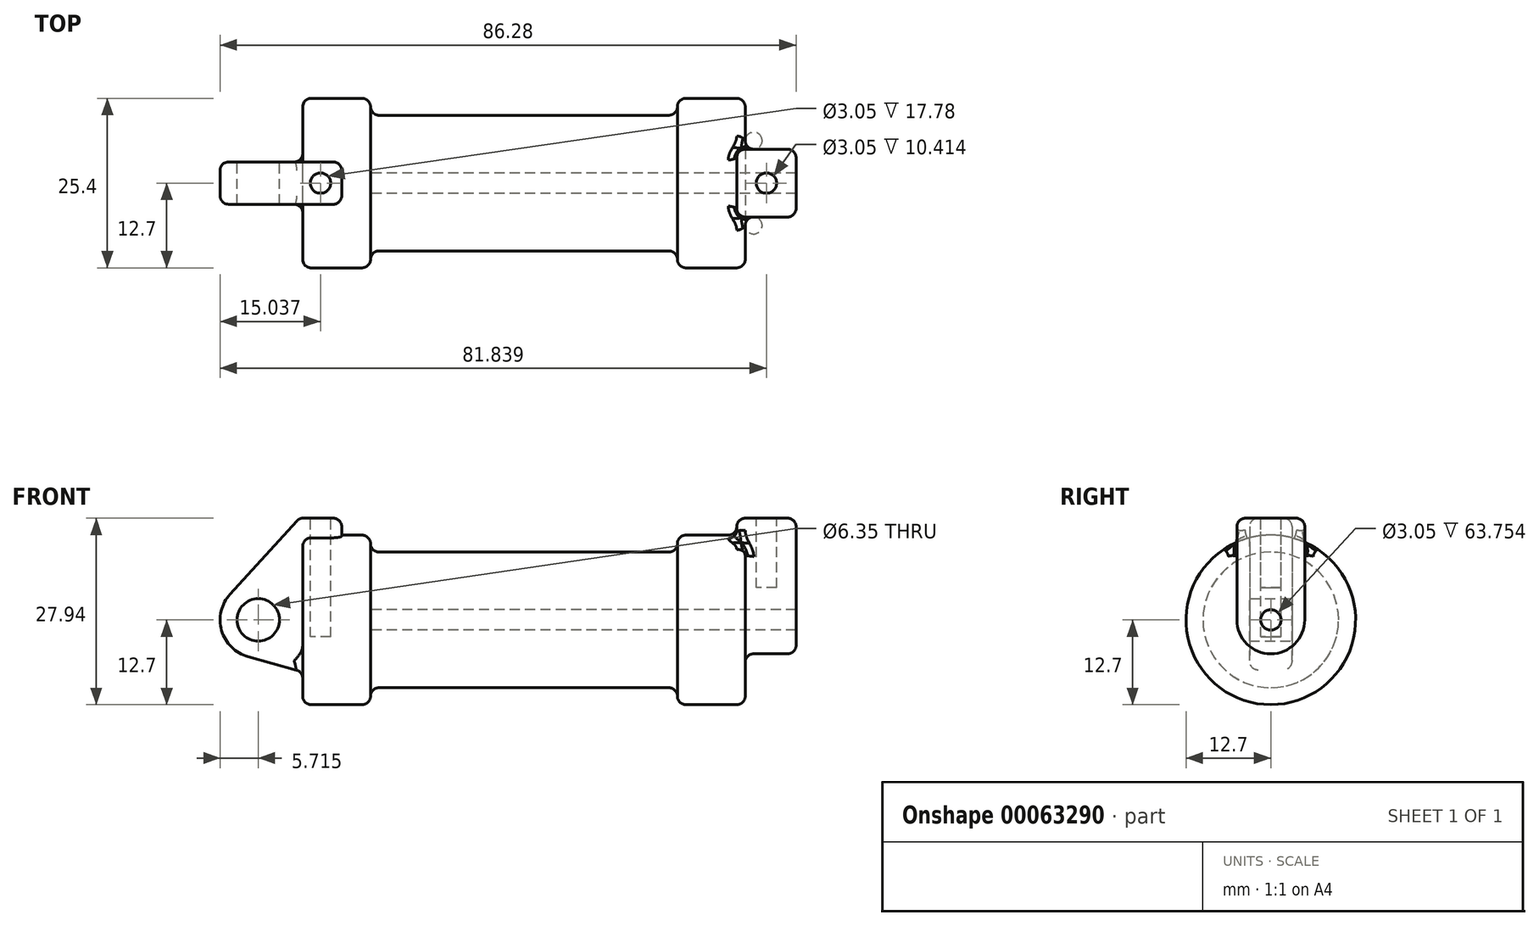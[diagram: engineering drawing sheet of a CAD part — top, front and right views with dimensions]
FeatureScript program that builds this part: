
annotation { "Feature Type Name" : "Feature", "Feature Type Description" : "" }
export const myFeature = defineFeature(function(context is Context, id is Id, definition is map)
    precondition{}
    {
        {
            var Q0;
            Q0=qCreatedBy(makeId("Front.planeOp"),FACE);
            var sketch = newSketch(context, id + "F0", { "sketchPlane" : qUnion([Q0])});
            skLineSegment(sketch, "E0", {"start": v(0, 0) * mm, "end": v(0, 12.7) * mm});
            skLineSegment(sketch, "E1", {"start": v(0, 12.7) * mm, "end": v(10.16, 12.7) * mm});
            skLineSegment(sketch, "E2", {"start": v(10.16, 12.7) * mm, "end": v(10.16, 10.16) * mm});
            skLineSegment(sketch, "E3", {"start": v(10.16, 10.16) * mm, "end": v(56.13, 10.16) * mm});
            skLineSegment(sketch, "E4", {"start": v(56.13, 10.16) * mm, "end": v(56.13, 12.7) * mm});
            skLineSegment(sketch, "E5", {"start": v(56.13, 12.7) * mm, "end": v(66.3, 12.7) * mm});
            skLineSegment(sketch, "E6", {"start": v(66.3, 12.7) * mm, "end": v(66.3, 0) * mm});
            skLineSegment(sketch, "E7", {"start": v(66.3, 0) * mm, "end": v(0, 0) * mm});
            skLineSegment(sketch, "E8", {"start": v(5.84, 15.24) * mm, "end": v(-0.5, 15.24) * mm});
            skLineSegment(sketch, "E9", {"start": v(-0.5, 15.24) * mm, "end": v(-10.88, 3.85) * mm});
            skLineSegment(sketch, "E10", {"start": v(0, 0) * mm, "end": v(-6.65, 0) * mm});
            skCircle(sketch, "E11", {"center": v(-6.65, 0) * mm, "radius": 5.72 * mm});
            skCircle(sketch, "E12", {"center": v(-6.65, 0) * mm, "radius": 3.18 * mm});
            skLineSegment(sketch, "E13", {"start": v(5.84, 15.24) * mm, "end": v(5.84, -9.4) * mm});
            skLineSegment(sketch, "E14", {"start": v(5.84, -9.4) * mm, "end": v(-8.18, -5.5) * mm});
            skSolve(sketch);
        }
        {
            var Q0;
            {var subQ0=sQuery(id+"F0.wireOp",EDGE,"E2");Q0=makeQuery(id+"F0.imprint","IMPRINT",FACE,{"disambiguationData":[TD([[makeQuery(id+"F0.imprint","IMPRINT",EDGE,{"derivedFrom":subQ0}),-1.0]])]});}
            var Q1;
            {var subQ0=sQuery(id+"F0.wireOp",EDGE,"E0");Q1=makeQuery(id+"F0.imprint","IMPRINT",FACE,{"disambiguationData":[TD([[makeQuery(id+"F0.imprint","IMPRINT",EDGE,{"derivedFrom":subQ0}),-1.0]])]});}
            var Q2;
            Q2=sQuery(id+"F0.wireOp",EDGE,"E0");
            var Q3;
            Q3=sQuery(id+"F0.wireOp",EDGE,"E1");
            var Q4;
            Q4=sQuery(id+"F0.wireOp",EDGE,"E4");
            var Q5;
            Q5=sQuery(id+"F0.wireOp",EDGE,"E5");
            var Q6;
            Q6=sQuery(id+"F0.wireOp",EDGE,"E6");
            var Q7;
            Q7=sQuery(id+"F0.wireOp",EDGE,"E2");
            var Q8;
            Q8=sQuery(id+"F0.wireOp",EDGE,"E3");
            var Q9;
            Q9=sQuery(id+"F0.wireOp",EDGE,"E7");
            var Q10;
            Q10=sQuery(id+"F0.wireOp",EDGE,"E7");
            revolve(context, id + "F1", {"entities" : qUnion([Q0, Q1]), "surfaceEntities" : qUnion([Q2, Q3, Q4, Q5, Q6, Q7, Q8, Q9]), "axis" : qUnion([Q10]), "revolveType" : RevolveType.FULL});
        }
        {
            var Q0;
            {var subQ3=sQuery(id+"F0.wireOp",EDGE,"E0");Q0=makeQuery(id+"F0.imprint","IMPRINT",FACE,{"disambiguationData":[TD([[makeQuery(id+"F0.imprint","IMPRINT",EDGE,{"derivedFrom":subQ3}),1.0]])]});}
            var Q1;
            {var subQ0=sQuery(id+"F0.wireOp",EDGE,"E14");Q1=makeQuery(id+"F0.imprint","IMPRINT",FACE,{"disambiguationData":[TD([[makeQuery(id+"F0.imprint","IMPRINT",EDGE,{"derivedFrom":subQ0}),-1.0]])]});}
            var Q2;
            {var subQ4=sQuery(id+"F0.wireOp",EDGE,"E12");Q2=makeQuery(id+"F0.imprint","IMPRINT",FACE,{"disambiguationData":[TD([[makeQuery(id+"F0.imprint","IMPRINT",EDGE,{"derivedFrom":subQ4}),-1.0]])]});}
            var Q3;
            {var subQ0=sQuery(id+"F0.wireOp",EDGE,"E0");Q3=makeQuery(id+"F0.imprint","IMPRINT",FACE,{"disambiguationData":[TD([[makeQuery(id+"F0.imprint","IMPRINT",EDGE,{"derivedFrom":subQ0}),-1.0]])]});}
            extrude(context, id + "F2", {"entities" : qUnion([Q0, Q1, Q2, Q3]), "operationType" : NewBodyOperationType.ADD, "endBound" : BoundingType.SYMMETRIC, "depth" : 6.35 * mm});
        }
        {
            var Q0;
            Q0=makeQuery(id+"F1.opRevolve","SWEPT_FACE",FACE,{"disambiguationData":[OSD([sQuery(id+"F0.wireOp",EDGE,"E6")])]});
            var sketch = newSketch(context, id + "F3", { "sketchPlane" : qUnion([Q0])});
            skCircle(sketch, "E15", {"center": v(0, 0) * mm, "radius": 1.52 * mm});
            skCircle(sketch, "E16", {"center": v(0, 0) * mm, "radius": 5.08 * mm});
            skLineSegment(sketch, "E17", {"start": v(-5.08, 0) * mm, "end": v(-5.08, 15.24) * mm});
            skLineSegment(sketch, "E18", {"start": v(5.08, 0) * mm, "end": v(5.08, 15.24) * mm});
            skLineSegment(sketch, "E19", {"start": v(-5.08, 15.24) * mm, "end": v(5.08, 15.24) * mm});
            skSolve(sketch);
        }
        {
            var Q0;
            Q0 = qSketchRegion(id + "F3", true);
            extrude(context, id + "F4", {"entities" : qUnion([Q0]), "operationType" : NewBodyOperationType.ADD, "depth" : 7.62 * mm});
        }
        {
            var Q0;
            Q0 = qSketchRegion(id + "F3", true);
            extrude(context, id + "F5", {"entities" : qUnion([Q0]), "operationType" : NewBodyOperationType.ADD, "oppositeDirection" : true, "depth" : 1.27 * mm});
        }
        {
            var Q0;
            Q0=makeQuery(id+"F3.imprint","IMPRINT",FACE,{"disambiguationData":[TD([[makeQuery(id+"F3.imprint","IMPRINT",EDGE,{"derivedFrom":sQuery(id+"F3.wireOp",EDGE,"E15")}),1.0]])]});
            var Q1;
            Q1=makeQuery(id+"F1.opRevolve","SWEPT_FACE",FACE,{"disambiguationData":[OSD([sQuery(id+"F0.wireOp",EDGE,"E2")])]});
            extrude(context, id + "F6", {"entities" : qUnion([Q0]), "operationType" : NewBodyOperationType.REMOVE, "endBound" : BoundingType.UP_TO_SURFACE, "oppositeDirection" : true, "endBoundEntityFace" : qUnion([Q1]), "depth" : 25.4 * mm});
        }
        {
            var Q0;
            Q0=makeQuery(id+"F2.opExtrude","SWEPT_FACE",FACE,{"disambiguationData":[OSD([sQuery(id+"F0.wireOp",EDGE,"E8")])]});
            var sketch = newSketch(context, id + "F7", { "sketchPlane" : qUnion([Q0])});
            skLineSegment(sketch, "E20", {"start": v(-0.5, 0) * mm, "end": v(5.84, 0) * mm, "construction": true});
            skLineSegment(sketch, "E21", {"start": v(2.67, -3.18) * mm, "end": v(2.67, 3.18) * mm, "construction": true});
            skCircle(sketch, "E22", {"center": v(2.67, 0) * mm, "radius": 1.52 * mm});
            skSolve(sketch);
        }
        {
            var Q0;
            Q0 = qSketchRegion(id + "F7", true);
            extrude(context, id + "F8", {"entities" : qUnion([Q0]), "operationType" : NewBodyOperationType.REMOVE, "oppositeDirection" : true, "depth" : 17.78 * mm});
        }
        {
            var Q0;
            {var subQ0=sQuery(id+"F3.wireOp",EDGE,"E19");Q0=makeQuery(id+"F5.boolean.opBoolean","MERGE",FACE,{"derivedFrom":[makeQuery(id+"F4.opExtrude","SWEPT_FACE",FACE,{"disambiguationData":[OSD([subQ0])]}),makeQuery(id+"F5.opExtrude","SWEPT_FACE",FACE,{"disambiguationData":[OSD([subQ0])]})]});}
            var sketch = newSketch(context, id + "F9", { "sketchPlane" : qUnion([Q0])});
            skLineSegment(sketch, "E23", {"start": v(65.02, 0) * mm, "end": v(73.91, 0) * mm, "construction": true});
            skCircle(sketch, "E24", {"center": v(69.47, 0) * mm, "radius": 1.52 * mm});
            skSolve(sketch);
        }
        {
            var Q0;
            Q0 = qSketchRegion(id + "F9", true);
            extrude(context, id + "F10", {"entities" : qUnion([Q0]), "operationType" : NewBodyOperationType.REMOVE, "oppositeDirection" : true, "depth" : 10.4 * mm});
        }
        {
            var Q0;
            Q0=makeQuery(id+"F1.opRevolve","SWEPT_EDGE",EDGE,{"disambiguationData":[OSD([sQuery(id+"F0.wireOp",EDGE,"E4"),sQuery(id+"F0.wireOp",EDGE,"E5")])]});
            var Q1;
            Q1=makeQuery(id+"F1.opRevolve","SWEPT_EDGE",EDGE,{"disambiguationData":[OSD([sQuery(id+"F0.wireOp",EDGE,"E3"),sQuery(id+"F0.wireOp",EDGE,"E4")])]});
            var Q2;
            Q2=makeQuery(id+"F1.opRevolve","SWEPT_EDGE",EDGE,{"disambiguationData":[OSD([sQuery(id+"F0.wireOp",EDGE,"E1"),sQuery(id+"F0.wireOp",EDGE,"E2")])]});
            var Q3;
            Q3=makeQuery(id+"F1.opRevolve","SWEPT_EDGE",EDGE,{"disambiguationData":[OSD([sQuery(id+"F0.wireOp",EDGE,"E2"),sQuery(id+"F0.wireOp",EDGE,"E3")])]});
            var Q4;
            Q4=makeQuery(id+"F4.boolean.opBoolean","SPLIT",EDGE,{"disambiguationData":[OD(1.0)],"derivedFrom":makeQuery(id+"F1.opRevolve","SWEPT_EDGE",EDGE,{"disambiguationData":[OSD([sQuery(id+"F0.wireOp",EDGE,"E5"),sQuery(id+"F0.wireOp",EDGE,"E6")])]})});
            var Q5;
            Q5=makeQuery(id+"F1.opRevolve","SWEPT_EDGE",EDGE,{"disambiguationData":[OSD([sQuery(id+"F0.wireOp",EDGE,"E0"),sQuery(id+"F0.wireOp",EDGE,"E1")])]});
            var Q6;
            Q6=makeQuery(id+"F4.opExtrude","SWEPT_EDGE",EDGE,{"disambiguationData":[OSD([sQuery(id+"F3.wireOp",EDGE,"E16"),sQuery(id+"F3.wireOp",EDGE,"E18")])]});
            var Q7;
            Q7=makeQuery(id+"F4.opExtrude","CAP_EDGE",EDGE,{"disambiguationData":[OSD([sQuery(id+"F3.wireOp",EDGE,"E18")])],"isStart":false});
            var Q8;
            {var subQ0=sQuery(id+"F3.wireOp",EDGE,"E18");Q8=makeQuery(id+"F5.boolean.opBoolean","MERGE",FACE,{"derivedFrom":[makeQuery(id+"F4.opExtrude","SWEPT_FACE",FACE,{"disambiguationData":[OSD([subQ0])]}),makeQuery(id+"F5.opExtrude","SWEPT_FACE",FACE,{"disambiguationData":[OSD([subQ0])]})]});}
            var Q9;
            Q9=makeQuery(id+"F4.opExtrude","CAP_EDGE",EDGE,{"disambiguationData":[OSD([sQuery(id+"F3.wireOp",EDGE,"E17")])],"isStart":false});
            var Q10;
            Q10=makeQuery(id+"F4.opExtrude","CAP_EDGE",EDGE,{"disambiguationData":[OSD([sQuery(id+"F3.wireOp",EDGE,"E16")])],"isStart":false});
            var Q11;
            Q11=makeQuery(id+"F4.opExtrude","CAP_EDGE",EDGE,{"disambiguationData":[OSD([sQuery(id+"F3.wireOp",EDGE,"E16")])],"isStart":true});
            var Q12;
            {var subQ0=sQuery(id+"F3.wireOp",EDGE,"E17");Q12=makeQuery(id+"F5.boolean.opBoolean","MERGE",FACE,{"derivedFrom":[makeQuery(id+"F4.opExtrude","SWEPT_FACE",FACE,{"disambiguationData":[OSD([subQ0])]}),makeQuery(id+"F5.opExtrude","SWEPT_FACE",FACE,{"disambiguationData":[OSD([subQ0])]})]});}
            var Q13;
            Q13=makeQuery(id+"F4.opExtrude","CAP_EDGE",EDGE,{"disambiguationData":[OSD([sQuery(id+"F3.wireOp",EDGE,"E19")])],"isStart":false});
            var Q14;
            Q14=makeQuery(id+"F5.opExtrude","CAP_EDGE",EDGE,{"disambiguationData":[OSD([sQuery(id+"F3.wireOp",EDGE,"E19")])],"isStart":false});
            var Q15;
            Q15=makeQuery(id+"F2.opExtrude","SWEPT_FACE",FACE,{"disambiguationData":[OSD([sQuery(id+"F0.wireOp",EDGE,"E9")])]});
            var Q16;
            Q16=makeQuery(id+"F2.opExtrude","SWEPT_FACE",FACE,{"disambiguationData":[OSD([sQuery(id+"F0.wireOp",EDGE,"E11")])]});
            var Q17;
            Q17=makeQuery(id+"F2.opExtrude","SWEPT_FACE",FACE,{"disambiguationData":[OSD([sQuery(id+"F0.wireOp",EDGE,"E14")])]});
            var Q18;
            Q18=makeQuery(id+"F2.opExtrude","CAP_EDGE",EDGE,{"disambiguationData":[OSD([sQuery(id+"F0.wireOp",EDGE,"E8")])],"isStart":true});
            var Q19;
            Q19=makeQuery(id+"F2.opExtrude","CAP_EDGE",EDGE,{"disambiguationData":[OSD([sQuery(id+"F0.wireOp",EDGE,"E13")])],"isStart":true});
            var Q20;
            Q20=makeQuery(id+"F2.opExtrude","CAP_EDGE",EDGE,{"disambiguationData":[OSD([sQuery(id+"F0.wireOp",EDGE,"E8")])],"isStart":false});
            var Q21;
            Q21=makeQuery(id+"F2.opExtrude","SWEPT_EDGE",EDGE,{"disambiguationData":[OSD([sQuery(id+"F0.wireOp",EDGE,"E8"),sQuery(id+"F0.wireOp",EDGE,"E13")])]});
            var Q22;
            Q22=makeQuery(id+"F2.opExtrude","CAP_EDGE",EDGE,{"disambiguationData":[OSD([sQuery(id+"F0.wireOp",EDGE,"E13")])],"isStart":false});
            var Q23;
            Q23=makeQuery(id+"F5.boolean.opBoolean","INTERSECT",EDGE,{"derivedFrom":[makeQuery(id+"F1.opRevolve","SWEPT_FACE",FACE,{"disambiguationData":[OSD([sQuery(id+"F0.wireOp",EDGE,"E5")])]}),makeQuery(id+"F5.opExtrude","CAP_FACE",FACE,{"disambiguationData":[OSD([sQuery(id+"F3.wireOp",EDGE,"E15"),sQuery(id+"F3.wireOp",EDGE,"E16"),sQuery(id+"F3.wireOp",EDGE,"E17"),sQuery(id+"F3.wireOp",EDGE,"E18"),sQuery(id+"F3.wireOp",EDGE,"E19")])],"isStart":false})]});
            fillet(context, id + "F11", {"entities" : qUnion([Q0, Q1, Q2, Q3, Q4, Q5, Q6, Q7, Q8, Q9, Q10, Q11, Q12, Q13, Q14, Q15, Q16, Q17, Q18, Q19, Q20, Q21, Q22, Q23]), "radius" : 1.27 * mm, "tangentPropagation" : true, "allowEdgeOverflow" : false});
        }
    });
